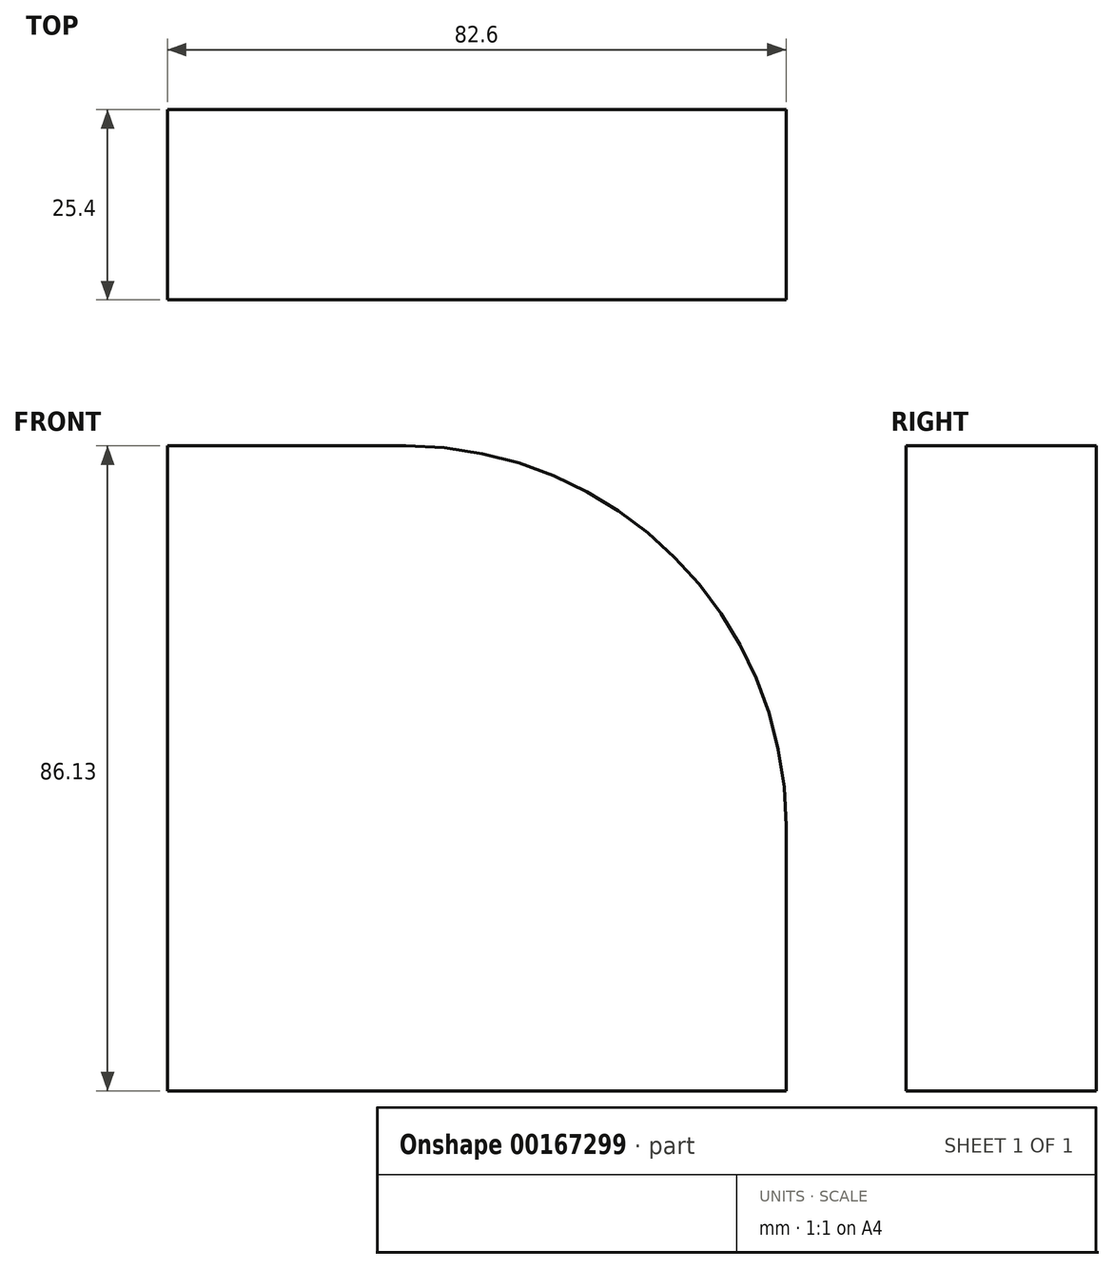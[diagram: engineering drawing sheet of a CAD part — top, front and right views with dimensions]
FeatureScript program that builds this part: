
annotation { "Feature Type Name" : "Feature", "Feature Type Description" : "" }
export const myFeature = defineFeature(function(context is Context, id is Id, definition is map)
    precondition{}
    {
        {
            var Q0;
            Q0=qCreatedBy(makeId("Front.planeOp"),FACE);
            var sketch = newSketch(context, id + "F0", { "sketchPlane" : qUnion([Q0])});
            skLineSegment(sketch, "E0.bottom", {"start": v(-64.05, -14.51) * mm, "end": v(-146.65, -14.51) * mm});
            skLineSegment(sketch, "E0.top", {"start": v(-64.05, -100.64) * mm, "end": v(-146.65, -100.64) * mm});
            skLineSegment(sketch, "E0.left", {"start": v(-64.05, -14.51) * mm, "end": v(-64.05, -100.64) * mm});
            skLineSegment(sketch, "E0.right", {"start": v(-146.65, -14.51) * mm, "end": v(-146.65, -100.64) * mm});
            skSolve(sketch);
        }
        {
            var Q0;
            Q0=qSketchRegion(id+"F0",true);
            extrude(context, id + "F1", {"entities" : qUnion([Q0]), "depth" : 25.4 * mm});
        }
        {
            var Q0;
            Q0=makeQuery(id+"F1.opExtrude","SWEPT_EDGE",EDGE,{"disambiguationData":[OSD([sQuery(id+"F0.wireOp",EDGE,"E0.bottom"),sQuery(id+"F0.wireOp",EDGE,"E0.left")])]});
            fillet(context, id + "F2", {"entities" : qUnion([Q0]), "radius" : 50.8 * mm, "tangentPropagation" : true, "allowEdgeOverflow" : false});
        }
    });
